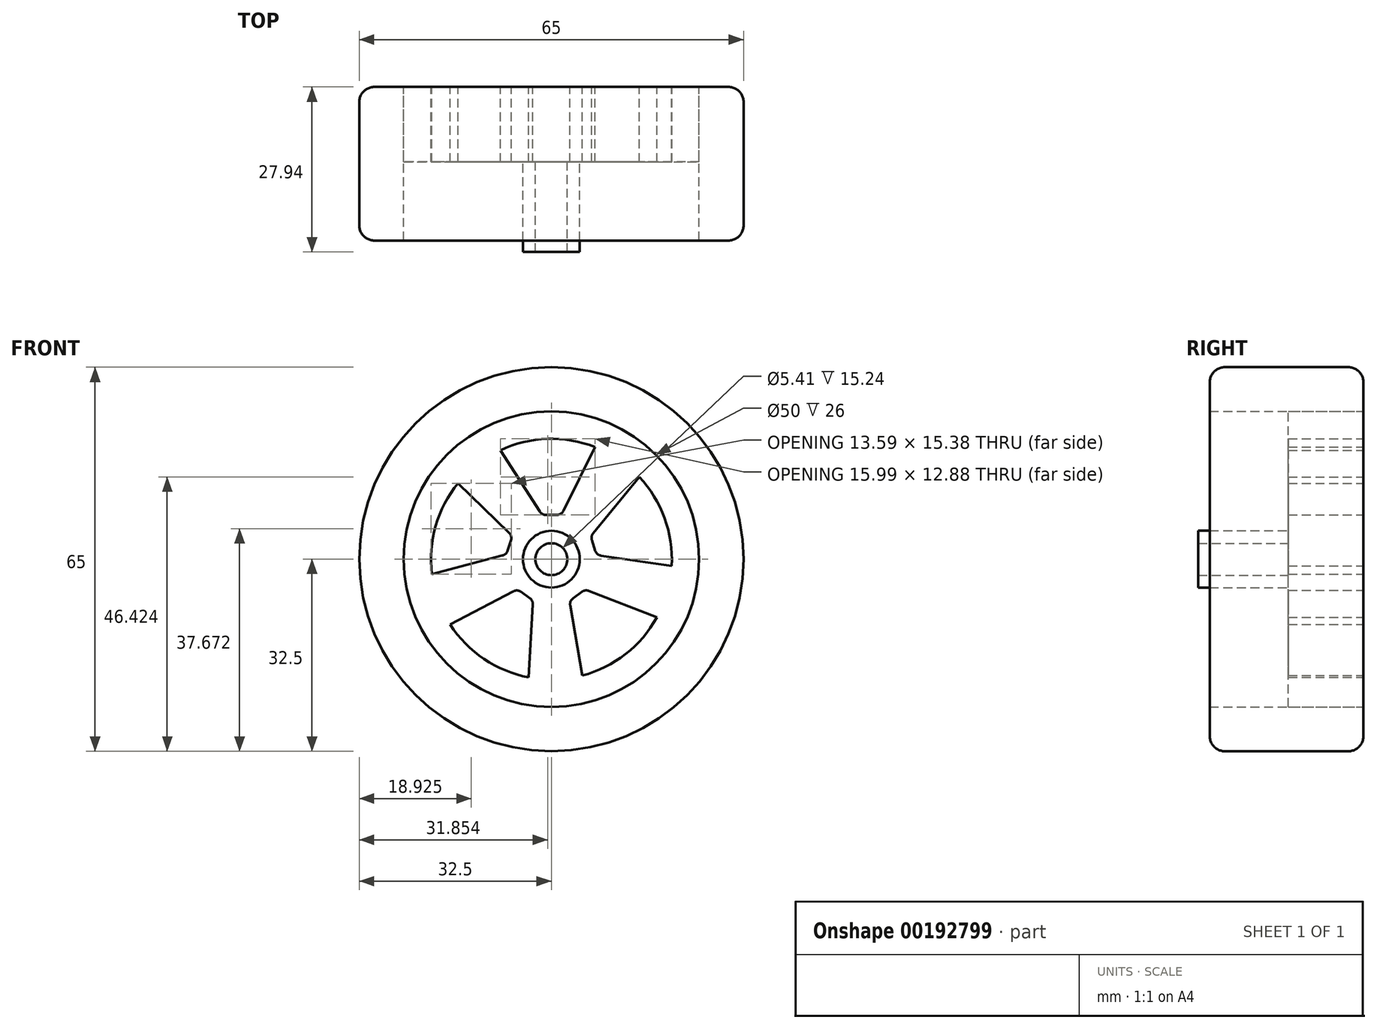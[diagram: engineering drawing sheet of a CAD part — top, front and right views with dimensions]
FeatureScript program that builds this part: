
annotation { "Feature Type Name" : "Feature", "Feature Type Description" : "" }
export const myFeature = defineFeature(function(context is Context, id is Id, definition is map)
    precondition{}
    {
        {
            var Q0;
            Q0=qCreatedBy(makeId("Front.planeOp"),FACE);
            var sketch = newSketch(context, id + "F0", { "sketchPlane" : qUnion([Q0])});
            skCircle(sketch, "E0", {"center": v(0, 0) * mm, "radius": 32.5 * mm});
            skCircle(sketch, "E1", {"center": v(0, 0) * mm, "radius": 25 * mm});
            skSolve(sketch);
        }
        {
            var Q0;
            Q0=makeQuery(id+"F0.imprint","IMPRINT",FACE,{"disambiguationData":[TD([[makeQuery(id+"F0.imprint","IMPRINT",EDGE,{"derivedFrom":sQuery(id+"F0.wireOp",EDGE,"E0")}),1.0]])]});
            extrude(context, id + "F1", {"entities" : qUnion([Q0]), "depth" : 26 * mm});
        }
        {
            var Q0;
            Q0=qCreatedBy(makeId("Front.planeOp"),FACE);
            var sketch = newSketch(context, id + "F2", { "sketchPlane" : qUnion([Q0])});
            skCircle(sketch, "E2.0", {"center": v(0, 0) * mm, "radius": 25 * mm});
            skArc(sketch, "E3", {"start": v(-15.8, 12.86) * mm, "mid": v(-19.58, 5.62) * mm, "end": v(-20.22, -2.52) * mm});
            skLineSegment(sketch, "E4", {"start": v(-8.64, 18.45) * mm, "end": v(-1.97, 8.07) * mm});
            skLineSegment(sketch, "E5", {"start": v(-0.9, 7.49) * mm, "end": v(0.9, 7.49) * mm});
            skLineSegment(sketch, "E6", {"start": v(2.03, 8.2) * mm, "end": v(7.35, 19) * mm});
            skPoint(sketch, "E7.visualSharp", {"position": v(-1.6, 7.49) * mm});
            skArc(sketch, "E7.filletArc", {"start": v(-1.97, 8.07) * mm, "mid": v(-1.51, 7.64) * mm, "end": v(-0.9, 7.49) * mm});
            skPoint(sketch, "E8.visualSharp", {"position": v(1.69, 7.49) * mm});
            skArc(sketch, "E8.filletArc", {"start": v(0.9, 7.49) * mm, "mid": v(1.57, 7.68) * mm, "end": v(2.03, 8.2) * mm});
            skPoint(sketch, "E9.1.0", {"position": v(-6.6, 3.92) * mm});
            skPoint(sketch, "E9.1.1", {"position": v(-7.61, 0.8) * mm});
            skLineSegment(sketch, "E9.1.2", {"start": v(-20.22, -2.52) * mm, "end": v(-8.28, 0.62) * mm});
            skLineSegment(sketch, "E9.1.3", {"start": v(-7.4, 1.45) * mm, "end": v(-6.84, 3.16) * mm});
            skLineSegment(sketch, "E9.1.4", {"start": v(-7.17, 4.47) * mm, "end": v(-15.8, 12.86) * mm});
            skArc(sketch, "E9.1.5", {"start": v(-8.28, 0.62) * mm, "mid": v(-7.73, 0.92) * mm, "end": v(-7.4, 1.45) * mm});
            skArc(sketch, "E9.1.6", {"start": v(-6.84, 3.16) * mm, "mid": v(-6.82, 3.86) * mm, "end": v(-7.17, 4.47) * mm});
            skPoint(sketch, "E9.2.0", {"position": v(-5.76, -5.07) * mm});
            skPoint(sketch, "E9.2.1", {"position": v(-3.1, -7) * mm});
            skLineSegment(sketch, "E9.2.2", {"start": v(-3.85, -20) * mm, "end": v(-3.15, -7.69) * mm});
            skLineSegment(sketch, "E9.2.3", {"start": v(-3.67, -6.59) * mm, "end": v(-5.12, -5.53) * mm});
            skLineSegment(sketch, "E9.2.4", {"start": v(-6.46, -5.43) * mm, "end": v(-17.12, -11.05) * mm});
            skArc(sketch, "E9.2.5", {"start": v(-3.15, -7.69) * mm, "mid": v(-3.27, -7.07) * mm, "end": v(-3.67, -6.59) * mm});
            skArc(sketch, "E9.2.6", {"start": v(-5.12, -5.53) * mm, "mid": v(-5.78, -5.3) * mm, "end": v(-6.46, -5.43) * mm});
            skPoint(sketch, "E9.3.0", {"position": v(3.04, -7.05) * mm});
            skPoint(sketch, "E9.3.1", {"position": v(5.7, -5.12) * mm});
            skLineSegment(sketch, "E9.3.2", {"start": v(17.84, -9.85) * mm, "end": v(6.34, -5.37) * mm});
            skLineSegment(sketch, "E9.3.3", {"start": v(5.13, -5.53) * mm, "end": v(3.68, -6.58) * mm});
            skLineSegment(sketch, "E9.3.4", {"start": v(3.17, -7.83) * mm, "end": v(5.22, -19.7) * mm});
            skArc(sketch, "E9.3.5", {"start": v(6.34, -5.37) * mm, "mid": v(5.71, -5.3) * mm, "end": v(5.13, -5.53) * mm});
            skArc(sketch, "E9.3.6", {"start": v(3.68, -6.58) * mm, "mid": v(3.25, -7.13) * mm, "end": v(3.17, -7.83) * mm});
            skPoint(sketch, "E9.4.0", {"position": v(7.64, 0.71) * mm});
            skPoint(sketch, "E9.4.1", {"position": v(6.63, 3.83) * mm});
            skLineSegment(sketch, "E9.4.2", {"start": v(14.88, 13.92) * mm, "end": v(7.07, 4.37) * mm});
            skLineSegment(sketch, "E9.4.3", {"start": v(6.84, 3.17) * mm, "end": v(7.4, 1.46) * mm});
            skLineSegment(sketch, "E9.4.4", {"start": v(8.42, 0.6) * mm, "end": v(20.34, -1.12) * mm});
            skArc(sketch, "E9.4.5", {"start": v(7.07, 4.37) * mm, "mid": v(6.8, 3.8) * mm, "end": v(6.84, 3.17) * mm});
            skArc(sketch, "E9.4.6", {"start": v(7.4, 1.46) * mm, "mid": v(7.79, 0.88) * mm, "end": v(8.42, 0.6) * mm});
            skArc(sketch, "E10.trimOffspring", {"start": v(7.35, 19) * mm, "mid": v(-0.7, 20.36) * mm, "end": v(-8.64, 18.45) * mm});
            skArc(sketch, "E11.trimOffspring", {"start": v(20.34, -1.12) * mm, "mid": v(19.15, 6.96) * mm, "end": v(14.88, 13.92) * mm});
            skArc(sketch, "E12.trimOffspring", {"start": v(5.22, -19.7) * mm, "mid": v(12.54, -16.06) * mm, "end": v(17.84, -9.85) * mm});
            skArc(sketch, "E13.trimOffspring", {"start": v(-17.12, -11.05) * mm, "mid": v(-11.4, -16.89) * mm, "end": v(-3.85, -20) * mm});
            skSolve(sketch);
        }
        {
            var Q0;
            Q0=qSketchRegion(id+"F2",true);
            extrude(context, id + "F3", {"entities" : qUnion([Q0]), "depth" : 12.7 * mm});
        }
        {
            var Q0;
            Q0=makeQuery(id+"F3.opExtrude","CAP_FACE",FACE,{"disambiguationData":[OSD([sQuery(id+"F2.wireOp",EDGE,"E2.0"),sQuery(id+"F2.wireOp",EDGE,"E3"),sQuery(id+"F2.wireOp",EDGE,"E4"),sQuery(id+"F2.wireOp",EDGE,"E5"),sQuery(id+"F2.wireOp",EDGE,"E6"),sQuery(id+"F2.wireOp",EDGE,"E7.filletArc"),sQuery(id+"F2.wireOp",EDGE,"E8.filletArc"),sQuery(id+"F2.wireOp",EDGE,"E9.1.2"),sQuery(id+"F2.wireOp",EDGE,"E9.1.3"),sQuery(id+"F2.wireOp",EDGE,"E9.1.4"),sQuery(id+"F2.wireOp",EDGE,"E9.1.5"),sQuery(id+"F2.wireOp",EDGE,"E9.1.6"),sQuery(id+"F2.wireOp",EDGE,"E9.2.2"),sQuery(id+"F2.wireOp",EDGE,"E9.2.3"),sQuery(id+"F2.wireOp",EDGE,"E9.2.4"),sQuery(id+"F2.wireOp",EDGE,"E9.2.5"),sQuery(id+"F2.wireOp",EDGE,"E9.2.6"),sQuery(id+"F2.wireOp",EDGE,"E9.3.2"),sQuery(id+"F2.wireOp",EDGE,"E9.3.3"),sQuery(id+"F2.wireOp",EDGE,"E9.3.4"),sQuery(id+"F2.wireOp",EDGE,"E9.3.5"),sQuery(id+"F2.wireOp",EDGE,"E9.3.6"),sQuery(id+"F2.wireOp",EDGE,"E9.4.2"),sQuery(id+"F2.wireOp",EDGE,"E9.4.3"),sQuery(id+"F2.wireOp",EDGE,"E9.4.4"),sQuery(id+"F2.wireOp",EDGE,"E9.4.5"),sQuery(id+"F2.wireOp",EDGE,"E9.4.6"),sQuery(id+"F2.wireOp",EDGE,"E10.trimOffspring"),sQuery(id+"F2.wireOp",EDGE,"E11.trimOffspring"),sQuery(id+"F2.wireOp",EDGE,"E12.trimOffspring"),sQuery(id+"F2.wireOp",EDGE,"E13.trimOffspring")])],"isStart":false});
            var sketch = newSketch(context, id + "F4", { "sketchPlane" : qUnion([Q0])});
            skCircle(sketch, "E14", {"center": v(0, 0) * mm, "radius": 4.8 * mm});
            skCircle(sketch, "E15", {"center": v(0, 0) * mm, "radius": 2.7 * mm});
            skSolve(sketch);
        }
        {
            var Q0;
            Q0=qSketchRegion(id+"F4",true);
            extrude(context, id + "F5", {"entities" : qUnion([Q0]), "operationType" : NewBodyOperationType.ADD, "depth" : 15.24 * mm});
        }
        {
            var Q0;
            Q0=makeQuery(id+"F1.opExtrude","CAP_EDGE",EDGE,{"disambiguationData":[OSD([sQuery(id+"F0.wireOp",EDGE,"E0")])],"isStart":false});
            var Q1;
            Q1=makeQuery(id+"F1.opExtrude","CAP_EDGE",EDGE,{"disambiguationData":[OSD([sQuery(id+"F0.wireOp",EDGE,"E0")])],"isStart":true});
            fillet(context, id + "F6", {"entities" : qUnion([Q0, Q1]), "radius" : 2.54 * mm, "tangentPropagation" : true, "allowEdgeOverflow" : false});
        }
    });
